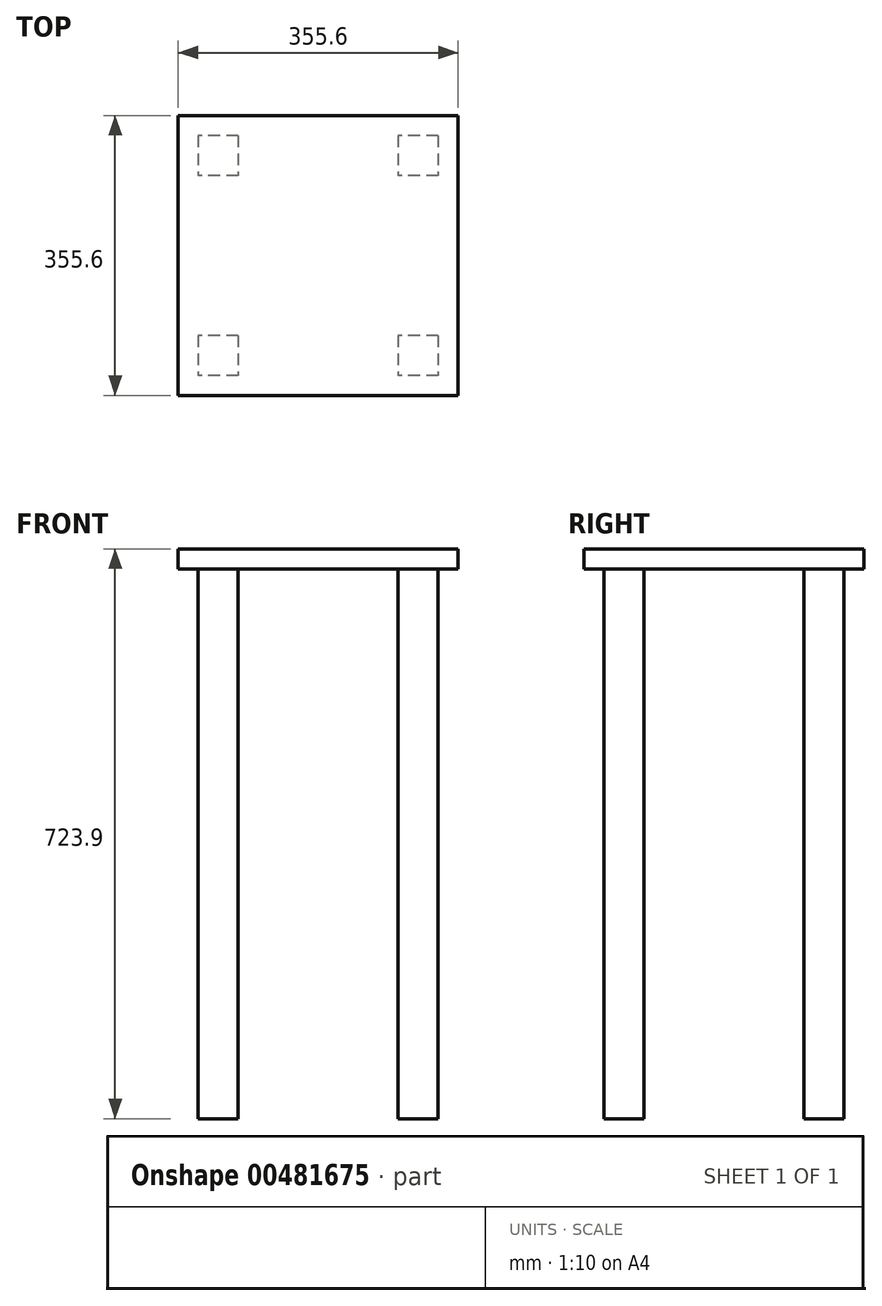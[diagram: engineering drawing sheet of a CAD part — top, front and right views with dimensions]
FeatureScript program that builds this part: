
annotation { "Feature Type Name" : "Feature", "Feature Type Description" : "" }
export const myFeature = defineFeature(function(context is Context, id is Id, definition is map)
    precondition{}
    {
        {
            var Q0;
            Q0=qCreatedBy(makeId("Top.planeOp"),FACE);
            var sketch = newSketch(context, id + "F0", { "sketchPlane" : qUnion([Q0])});
            skLineSegment(sketch, "E0.bottom", {"start": v(177.8, 177.8) * mm, "end": v(-177.8, 177.8) * mm});
            skLineSegment(sketch, "E0.top", {"start": v(177.8, -177.8) * mm, "end": v(-177.8, -177.8) * mm});
            skLineSegment(sketch, "E0.left", {"start": v(177.8, 177.8) * mm, "end": v(177.8, -177.8) * mm});
            skLineSegment(sketch, "E0.right", {"start": v(-177.8, 177.8) * mm, "end": v(-177.8, -177.8) * mm});
            skPoint(sketch, "E0.middle", {"position": v(0, 0) * mm});
            skSolve(sketch);
        }
        {
            var Q0;
            Q0 = qSketchRegion(id + "F0", true);
            extrude(context, id + "F1", {"entities" : qUnion([Q0]), "depth" : 25.4 * mm});
        }
        {
            var Q0;
            Q0=makeQuery(id+"F1.opExtrude","CAP_FACE",FACE,{"disambiguationData":[OSD([sQuery(id+"F0.wireOp",EDGE,"E0.bottom"),sQuery(id+"F0.wireOp",EDGE,"E0.top"),sQuery(id+"F0.wireOp",EDGE,"E0.left"),sQuery(id+"F0.wireOp",EDGE,"E0.right")])],"isStart":true});
            var sketch = newSketch(context, id + "F2", { "sketchPlane" : qUnion([Q0])});
            skLineSegment(sketch, "E1.bottom", {"start": v(-101.6, 101.6) * mm, "end": v(-152.4, 101.6) * mm});
            skLineSegment(sketch, "E1.top", {"start": v(-101.6, 152.4) * mm, "end": v(-152.4, 152.4) * mm});
            skLineSegment(sketch, "E1.left", {"start": v(-101.6, 101.6) * mm, "end": v(-101.6, 152.4) * mm});
            skLineSegment(sketch, "E1.right", {"start": v(-152.4, 101.6) * mm, "end": v(-152.4, 152.4) * mm});
            skPoint(sketch, "E1.middle", {"position": v(-127, 127) * mm});
            skPoint(sketch, "E2.0.1.0", {"position": v(-127, -127) * mm});
            skLineSegment(sketch, "E2.0.1.1", {"start": v(-101.6, -152.4) * mm, "end": v(-152.4, -152.4) * mm});
            skLineSegment(sketch, "E2.0.1.2", {"start": v(-101.6, -101.6) * mm, "end": v(-152.4, -101.6) * mm});
            skLineSegment(sketch, "E2.0.1.3", {"start": v(-101.6, -152.4) * mm, "end": v(-101.6, -101.6) * mm});
            skLineSegment(sketch, "E2.0.1.4", {"start": v(-152.4, -152.4) * mm, "end": v(-152.4, -101.6) * mm});
            skPoint(sketch, "E2.1.0.0", {"position": v(127, 127) * mm});
            skLineSegment(sketch, "E2.1.0.1", {"start": v(152.4, 101.6) * mm, "end": v(101.6, 101.6) * mm});
            skLineSegment(sketch, "E2.1.0.2", {"start": v(152.4, 152.4) * mm, "end": v(101.6, 152.4) * mm});
            skLineSegment(sketch, "E2.1.0.3", {"start": v(152.4, 101.6) * mm, "end": v(152.4, 152.4) * mm});
            skLineSegment(sketch, "E2.1.0.4", {"start": v(101.6, 101.6) * mm, "end": v(101.6, 152.4) * mm});
            skPoint(sketch, "E2.1.1.0", {"position": v(127, -127) * mm});
            skLineSegment(sketch, "E2.1.1.1", {"start": v(152.4, -152.4) * mm, "end": v(101.6, -152.4) * mm});
            skLineSegment(sketch, "E2.1.1.2", {"start": v(152.4, -101.6) * mm, "end": v(101.6, -101.6) * mm});
            skLineSegment(sketch, "E2.1.1.3", {"start": v(152.4, -152.4) * mm, "end": v(152.4, -101.6) * mm});
            skLineSegment(sketch, "E2.1.1.4", {"start": v(101.6, -152.4) * mm, "end": v(101.6, -101.6) * mm});
            skLineSegment(sketch, "E2.direction1", {"start": v(-152.4, 101.6) * mm, "end": v(101.6, 101.6) * mm, "construction": true});
            skLineSegment(sketch, "E2.direction2", {"start": v(-152.4, 101.6) * mm, "end": v(-152.4, -152.4) * mm, "construction": true});
            skSolve(sketch);
        }
        {
            var Q0;
            Q0 = qSketchRegion(id + "F2", true);
            extrude(context, id + "F3", {"entities" : qUnion([Q0]), "operationType" : NewBodyOperationType.ADD, "depth" : 698.5 * mm});
        }
    });
